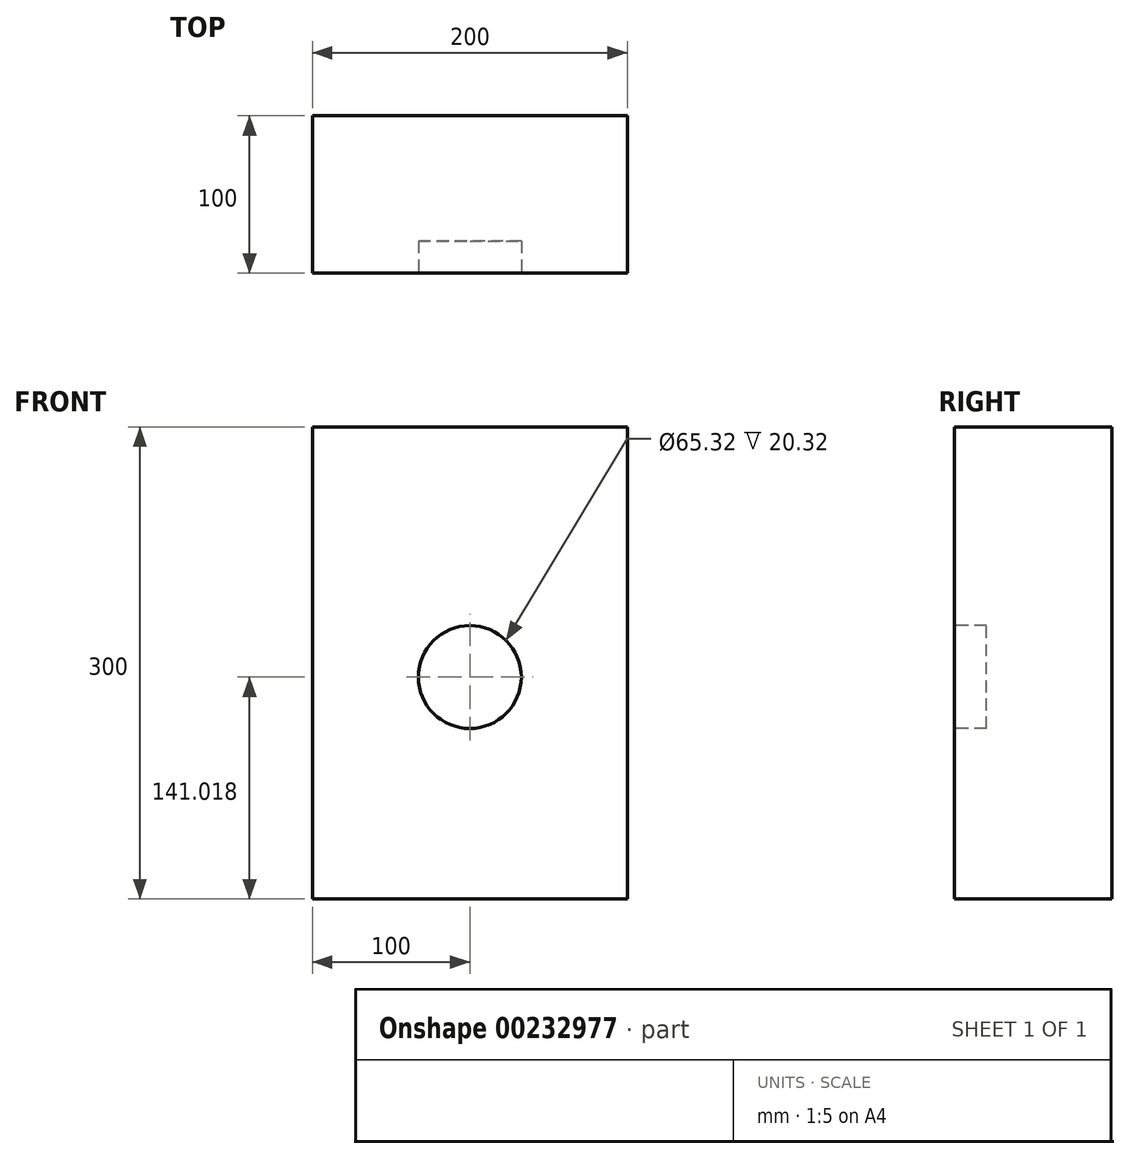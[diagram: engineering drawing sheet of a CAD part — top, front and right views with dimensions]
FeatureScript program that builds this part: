
annotation { "Feature Type Name" : "Feature", "Feature Type Description" : "" }
export const myFeature = defineFeature(function(context is Context, id is Id, definition is map)
    precondition{}
    {
        {
            var Q0;
            Q0=qCreatedBy(makeId("Top.planeOp"),FACE);
            var sketch = newSketch(context, id + "F0", { "sketchPlane" : qUnion([Q0])});
            skLineSegment(sketch, "E0.bottom", {"start": v(100, 50) * mm, "end": v(-100, 50) * mm});
            skLineSegment(sketch, "E0.top", {"start": v(100, -50) * mm, "end": v(-100, -50) * mm});
            skLineSegment(sketch, "E0.left", {"start": v(100, 50) * mm, "end": v(100, -50) * mm});
            skLineSegment(sketch, "E0.right", {"start": v(-100, 50) * mm, "end": v(-100, -50) * mm});
            skPoint(sketch, "E0.middle", {"position": v(0, 0) * mm});
            skSolve(sketch);
        }
        {
            var Q0;
            Q0=makeQuery(id+"F0.imprint","IMPRINT",FACE,{"disambiguationData":[TD([[makeQuery(id+"F0.imprint","IMPRINT",EDGE,{"derivedFrom":sQuery(id+"F0.wireOp",EDGE,"E0.bottom")}),1.0]])]});
            extrude(context, id + "F1", {"entities" : qUnion([Q0]), "oppositeDirection" : true, "depth" : 300 * mm});
        }
        {
            var Q0;
            Q0=makeQuery(id+"F1.opExtrude","SWEPT_FACE",FACE,{"disambiguationData":[OSD([sQuery(id+"F0.wireOp",EDGE,"E0.top")])]});
            var sketch = newSketch(context, id + "F2", { "sketchPlane" : qUnion([Q0])});
            skCircle(sketch, "E1", {"center": v(0, -158.98) * mm, "radius": 32.66 * mm});
            skSolve(sketch);
        }
        {
            var Q0;
            Q0=makeQuery(id+"F2.imprint","IMPRINT",FACE,{"disambiguationData":[TD([[makeQuery(id+"F2.imprint","IMPRINT",EDGE,{"derivedFrom":sQuery(id+"F2.wireOp",EDGE,"E1")}),1.0]])]});
            extrude(context, id + "F3", {"entities" : qUnion([Q0]), "operationType" : NewBodyOperationType.REMOVE, "oppositeDirection" : true, "depth" : 20.32 * mm});
        }
    });
